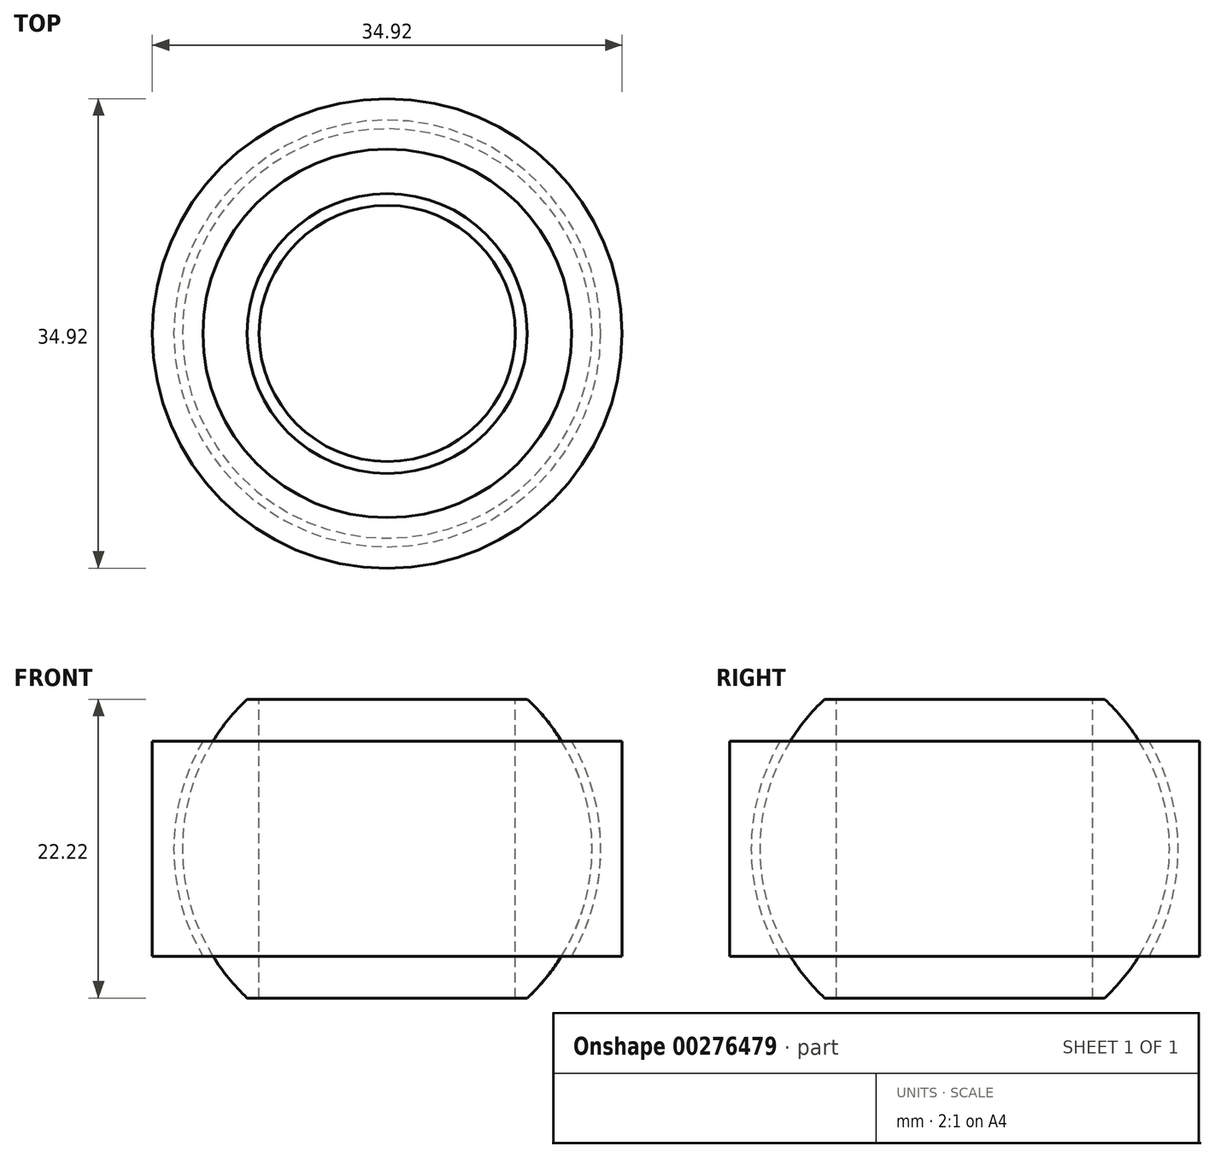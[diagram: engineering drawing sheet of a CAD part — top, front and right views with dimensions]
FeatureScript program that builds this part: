
annotation { "Feature Type Name" : "Feature", "Feature Type Description" : "" }
export const myFeature = defineFeature(function(context is Context, id is Id, definition is map)
    precondition{}
    {
        {
            var Q0;
            Q0=qCreatedBy(makeId("Front.planeOp"),FACE);
            var sketch = newSketch(context, id + "F0", { "sketchPlane" : qUnion([Q0])});
            skLineSegment(sketch, "E0", {"start": v(9.52, 11.11) * mm, "end": v(9.53, -11.11) * mm});
            skLineSegment(sketch, "E1", {"start": v(9.53, -11.11) * mm, "end": v(10.4, -11.11) * mm});
            skLineSegment(sketch, "E2", {"start": v(9.52, 11.11) * mm, "end": v(10.4, 11.11) * mm});
            skLineSegment(sketch, "E3", {"start": v(12.93, 8) * mm, "end": v(12.95, 8) * mm});
            skLineSegment(sketch, "E4", {"start": v(17.46, 8) * mm, "end": v(17.46, -8) * mm});
            skLineSegment(sketch, "E5", {"start": v(17.46, -8) * mm, "end": v(13.7, -8) * mm});
            skArc(sketch, "E6", {"start": v(10.4, -11.11) * mm, "mid": v(15.23, 0) * mm, "end": v(10.4, 11.11) * mm});
            skLineSegment(sketch, "E7", {"start": v(0, 0) * mm, "end": v(0, -25.52) * mm, "construction": true});
            skLineSegment(sketch, "E8.trimOffspring", {"start": v(13.7, 8) * mm, "end": v(17.46, 8) * mm});
            skArc(sketch, "E9.trimOffspring", {"start": v(13.7, -8) * mm, "mid": v(15.87, 0) * mm, "end": v(13.7, 8) * mm});
            skSolve(sketch);
        }
        {
            var Q0;
            Q0=makeQuery(id+"F0.imprint","IMPRINT",FACE,{"disambiguationData":[TD([[makeQuery(id+"F0.imprint","IMPRINT",EDGE,{"derivedFrom":sQuery(id+"F0.wireOp",EDGE,"E0")}),1.0]])]});
            var Q1;
            Q1=makeQuery(id+"F0.imprint","IMPRINT",FACE,{"disambiguationData":[TD([[makeQuery(id+"F0.imprint","IMPRINT",EDGE,{"derivedFrom":sQuery(id+"F0.wireOp",EDGE,"E4")}),-1.0]])]});
            var Q2;
            Q2=sQuery(id+"F0.wireOp",EDGE,"E7");
            revolve(context, id + "F1", {"entities" : qUnion([Q0, Q1]), "axis" : qUnion([Q2]), "revolveType" : RevolveType.FULL});
        }
    });
